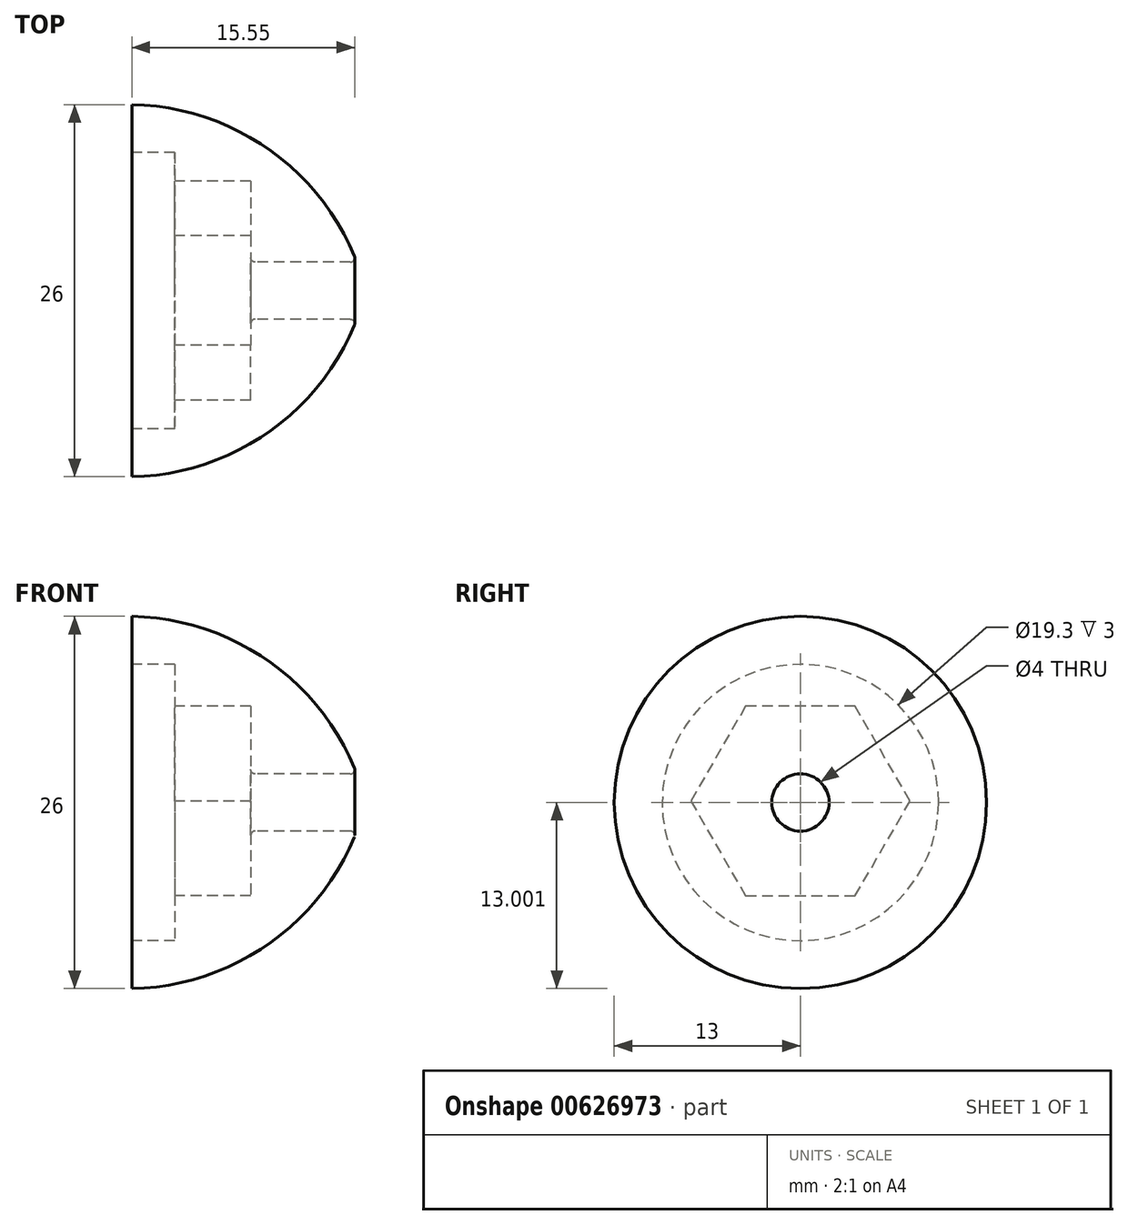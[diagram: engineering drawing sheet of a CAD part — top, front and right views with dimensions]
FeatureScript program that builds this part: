
annotation { "Feature Type Name" : "Feature", "Feature Type Description" : "" }
export const myFeature = defineFeature(function(context is Context, id is Id, definition is map)
    precondition{}
    {
        {
            var Q0;
            Q0=qCreatedBy(makeId("Front.planeOp"),FACE);
            var sketch = newSketch(context, id + "F0", { "sketchPlane" : qUnion([Q0])});
            skLineSegment(sketch, "E0", {"start": v(-12.67, 12.9) * mm, "end": v(-12.67, 9.55) * mm});
            skLineSegment(sketch, "E1", {"start": v(-12.67, 9.55) * mm, "end": v(-9.67, 9.55) * mm});
            skLineSegment(sketch, "E2", {"start": v(-9.67, 9.55) * mm, "end": v(-9.67, 3.55) * mm});
            skLineSegment(sketch, "E3", {"start": v(-9.67, 3.55) * mm, "end": v(-4.37, 3.55) * mm});
            skLineSegment(sketch, "E4", {"start": v(-4.37, 3.55) * mm, "end": v(-4.37, 1.9) * mm});
            skLineSegment(sketch, "E5", {"start": v(-4.37, 1.9) * mm, "end": v(3.03, 1.9) * mm});
            skArc(sketch, "E6", {"start": v(3.03, 1.9) * mm, "mid": v(-3.15, 9.79) * mm, "end": v(-12.67, 12.9) * mm});
            skLineSegment(sketch, "E7", {"start": v(-26.48, -0.1) * mm, "end": v(12.43, -0.1) * mm, "construction": true});
            skSolve(sketch);
        }
        {
            var Q0;
            Q0 = qSketchRegion(id + "F0", true);
            var Q1;
            Q1=sQuery(id+"F0.wireOp",EDGE,"E7");
            revolve(context, id + "F1", {"entities" : qUnion([Q0]), "axis" : qUnion([Q1]), "revolveType" : RevolveType.FULL});
        }
        {
            var Q0;
            Q0=makeQuery(id+"F1.opRevolve","SWEPT_EDGE",EDGE,{"disambiguationData":[OSD([sQuery(id+"F0.wireOp",EDGE,"E4"),sQuery(id+"F0.wireOp",EDGE,"E5")])]});
            var Q1;
            Q1=makeQuery(id+"F1.opRevolve","SWEPT_EDGE",EDGE,{"disambiguationData":[OSD([sQuery(id+"F0.wireOp",EDGE,"E5"),sQuery(id+"F0.wireOp",EDGE,"E6")])]});
            fillet(context, id + "F2", {"entities" : qUnion([Q0, Q1]), "radius" : 0.3 * mm, "tangentPropagation" : true, "allowEdgeOverflow" : false});
        }
        {
            var Q0;
            Q0=makeQuery(id+"F1.opRevolve","SWEPT_FACE",FACE,{"disambiguationData":[OSD([sQuery(id+"F0.wireOp",EDGE,"E2")])]});
            var sketch = newSketch(context, id + "F3", { "sketchPlane" : qUnion([Q0])});
            skCircle(sketch, "E8.cCircle", {"center": v(0, 0) * mm, "radius": 7.65 * mm, "construction": true});
            skLineSegment(sketch, "E8.0", {"start": v(7.65, 0) * mm, "end": v(3.82, -6.63) * mm});
            skLineSegment(sketch, "E8.1", {"start": v(3.83, -6.63) * mm, "end": v(-3.82, -6.63) * mm});
            skLineSegment(sketch, "E8.2", {"start": v(-3.82, -6.63) * mm, "end": v(-7.65, 0) * mm});
            skLineSegment(sketch, "E8.3", {"start": v(-7.65, 0) * mm, "end": v(-3.83, 6.63) * mm});
            skLineSegment(sketch, "E8.4", {"start": v(-3.83, 6.63) * mm, "end": v(3.82, 6.63) * mm});
            skLineSegment(sketch, "E8.5", {"start": v(3.82, 6.63) * mm, "end": v(7.65, 0) * mm});
            skSolve(sketch);
        }
        {
            var Q0;
            Q0=makeQuery(id+"F3.imprint","IMPRINT",FACE,{"disambiguationData":[TD([[makeQuery(id+"F3.imprint","IMPRINT",EDGE,{"derivedFrom":sQuery(id+"F3.wireOp",EDGE,"E8.0")}),-1.0]])]});
            extrude(context, id + "F4", {"entities" : qUnion([Q0]), "operationType" : NewBodyOperationType.REMOVE, "oppositeDirection" : true, "depth" : 5.3 * mm, "offsetDistance" : 25 * mm});
        }
    });
